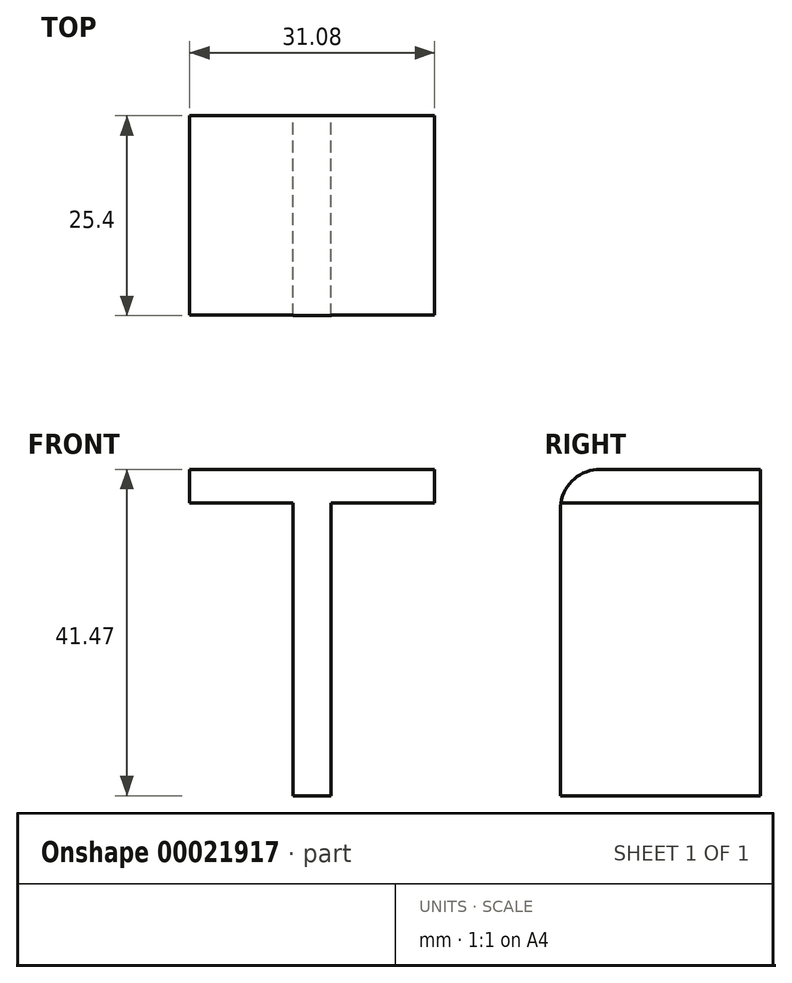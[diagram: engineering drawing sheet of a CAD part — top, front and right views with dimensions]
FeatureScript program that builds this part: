
annotation { "Feature Type Name" : "Feature", "Feature Type Description" : "" }
export const myFeature = defineFeature(function(context is Context, id is Id, definition is map)
    precondition{}
    {
        {
            var Q0;
            Q0=qCreatedBy(makeId("Front.planeOp"),FACE);
            var sketch = newSketch(context, id + "F0", { "sketchPlane" : qUnion([Q0])});
            skText(sketch, "E0", { "text": "TOTO", "fontName": "OpenSans-Regular.ttf"});
            const initialGuessF0  = {"E0": [-0.07147, 0.00885, 1, 0, 0.04182]};
            skSetInitialGuess(sketch, initialGuessF0);
            skSolve(sketch);
        }
        {
            var Q0;
            Q0=makeQuery(id+"F0.imprint","IMPRINT",FACE,{"disambiguationData":[TD([[makeQuery(id+"F0.imprint","IMPRINT",EDGE,{"derivedFrom":sQuery(id+"F0.wireOp",EDGE,"E0.sketch_text.stroke-0")}),-1.0]])]});
            extrude(context, id + "F1", {"entities" : qUnion([Q0]), "depth" : 25.4 * mm});
        }
        {
            var Q0;
            Q0=makeQuery(id+"F1.opExtrude","CAP_EDGE",EDGE,{"disambiguationData":[OSD([sQuery(id+"F0.wireOp",EDGE,"E0.sketch_text.stroke-4")])],"isStart":false});
            fillet(context, id + "F2", {"entities" : qUnion([Q0]), "radius" : 5.08 * mm, "tangentPropagation" : true, "allowEdgeOverflow" : false});
        }
    });
